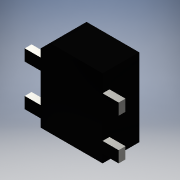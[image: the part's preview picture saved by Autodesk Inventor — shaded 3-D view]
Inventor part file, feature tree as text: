
AUTODESK INVENTOR PART (.ipt)
format: ipt  version: 2016 (Build 200138000, 138)  size: 123,904 bytes
history: native  units: mm
features: extrude x2, sketch x2, pattern_linear x1
ambient origin geometry x8: Origin, YZ Plane, XZ Plane, XY Plane, X Axis, Y Axis, Z Axis, Center Point
bodies: Solid1 (feature_tree)
feature tree (5):
  extrude  "Extrusion1"  Depth=2.3mm
  extrude  "Extrusion2"  Depth=0.5mm
  pattern_linear  "Rectangular Pattern1"  Spacing1=0.3mm  [1 undecoded]
  sketch  "Sketch1"  dims[d2=45.0deg d3=2.3mm]
  sketch  "Sketch2"  dims[d5=0.0mm d6=0.5mm d7=0.3mm d8=0.9mm d10=0.7mm d11=0.0mm d12=20.0mm d14=1.8mm d15=20.0mm d17=3.4mm]
note: 1 required parameter value undecoded (feature->parameter linkage not recoverable at this tier; creation-order binding heuristic only, values carry confidence <= 0.55)
